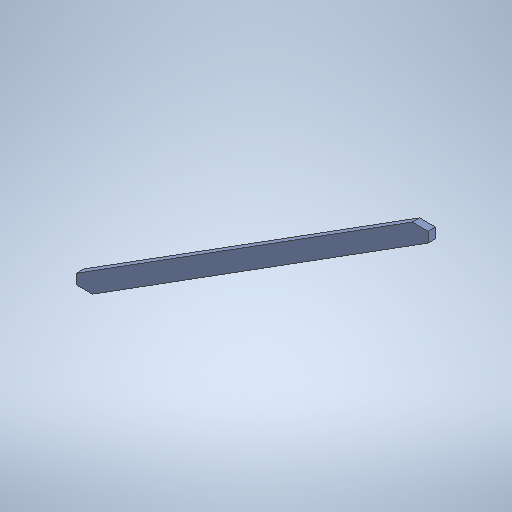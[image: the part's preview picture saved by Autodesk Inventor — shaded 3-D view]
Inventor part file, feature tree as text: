
AUTODESK INVENTOR PART (.ipt)
format: ipt  version: 2025.1 (Build 291241020, 241B)  size: 253,952 bytes
history: native  units: in
note: dims shown in document units (in); Inventor stores cm internally (conversion verified against a paired STEP export)
features: other x7, reference x4, extrude x1, sketch x1
ambient origin geometry x8: Origin, YZ Plane, XZ Plane, XY Plane, X Axis, Y Axis, Z Axis, Center Point
bodies: Solid1 (feature_tree)
feature tree (13):
  extrude  "Extrusion1"  [1 undecoded]
  sketch  "Sketch1"  dims[d2=1.5in d3=0.0in]
  reference  "Reference1"
  reference  "Reference2"
  reference  "Reference3"
  reference  "Reference4"
  other  "<userpath>\Documents\Tburn24\Assembly1.iam"
  other  "Assembly1.iam"
  other  "6'x4x4:22"
  other  "16'x2x4:2"
  other  "16'x4x4:1"
  other  "6'x2x4:1"
  other  "Finish1"
note: 1 required parameter value undecoded (feature->parameter linkage not recoverable at this tier; creation-order binding heuristic only, values carry confidence <= 0.55)
